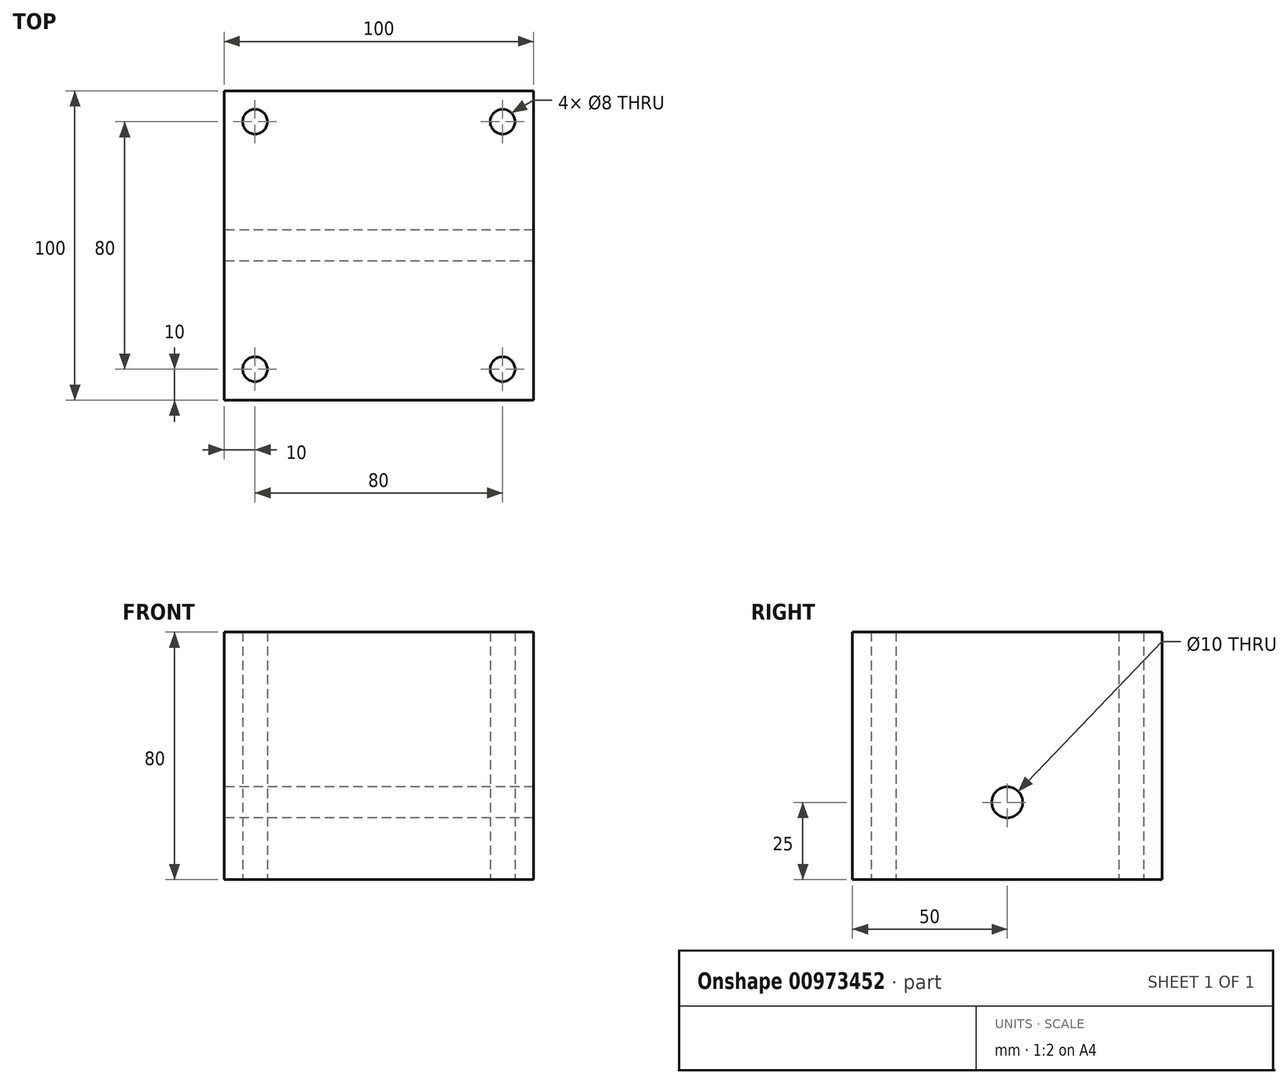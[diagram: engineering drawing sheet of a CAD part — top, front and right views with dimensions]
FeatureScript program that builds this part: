
annotation { "Feature Type Name" : "Feature", "Feature Type Description" : "" }
export const myFeature = defineFeature(function(context is Context, id is Id, definition is map)
    precondition{}
    {
        {
            var Q0;
            Q0=qCreatedBy(makeId("Top.planeOp"),FACE);
            var sketch = newSketch(context, id + "F0", { "sketchPlane" : qUnion([Q0])});
            skLineSegment(sketch, "E0.bottom", {"start": v(-50, 50) * mm, "end": v(50, 50) * mm});
            skLineSegment(sketch, "E0.top", {"start": v(-50, -50) * mm, "end": v(50, -50) * mm});
            skLineSegment(sketch, "E0.left", {"start": v(-50, 50) * mm, "end": v(-50, -50) * mm});
            skLineSegment(sketch, "E0.right", {"start": v(50, 50) * mm, "end": v(50, -50) * mm});
            skPoint(sketch, "E0.middle", {"position": v(0, 0) * mm});
            skSolve(sketch);
        }
        {
            var Q0;
            Q0=makeQuery(id+"F0.imprint","IMPRINT",FACE,{"disambiguationData":[TD([[makeQuery(id+"F0.imprint","IMPRINT",EDGE,{"derivedFrom":sQuery(id+"F0.wireOp",EDGE,"E0.bottom")}),-1.0]])]});
            extrude(context, id + "F1", {"entities" : qUnion([Q0]), "depth" : 50 * mm, "offsetDistance" : 25 * mm});
        }
        {
            var Q0;
            Q0=makeQuery(id+"F1.opExtrude","CAP_FACE",FACE,{"disambiguationData":[OSD([sQuery(id+"F0.wireOp",EDGE,"E0.bottom"),sQuery(id+"F0.wireOp",EDGE,"E0.top"),sQuery(id+"F0.wireOp",EDGE,"E0.left"),sQuery(id+"F0.wireOp",EDGE,"E0.right")])],"isStart":false});
            var sketch = newSketch(context, id + "F2", { "sketchPlane" : qUnion([Q0])});
            skCircle(sketch, "E1", {"center": v(-40, 40) * mm, "radius": 4 * mm});
            skCircle(sketch, "E2", {"center": v(40, 40) * mm, "radius": 4 * mm});
            skCircle(sketch, "E3", {"center": v(-40, -40) * mm, "radius": 4 * mm});
            skCircle(sketch, "E4", {"center": v(40, -40) * mm, "radius": 4 * mm});
            skSolve(sketch);
        }
        {
            var Q0;
            Q0=makeQuery(id+"F2.imprint","IMPRINT",FACE,{"disambiguationData":[TD([[makeQuery(id+"F2.imprint","IMPRINT",EDGE,{"derivedFrom":sQuery(id+"F2.wireOp",EDGE,"E1")}),-1.0]])]});
            extrude(context, id + "F3", {"entities" : qUnion([Q0]), "operationType" : NewBodyOperationType.ADD, "depth" : 30 * mm, "offsetDistance" : 25 * mm});
        }
        {
            var Q0;
            Q0=makeQuery(id+"F3.boolean.opBoolean","SPLIT",FACE,{"disambiguationData":[TD([makeQuery(id+"F3.opExtrude","SWEPT_FACE",FACE,{"disambiguationData":[OSD([sQuery(id+"F2.wireOp",EDGE,"E1")])]})])],"derivedFrom":makeQuery(id+"F1.opExtrude","CAP_FACE",FACE,{"disambiguationData":[OSD([sQuery(id+"F0.wireOp",EDGE,"E0.bottom"),sQuery(id+"F0.wireOp",EDGE,"E0.top"),sQuery(id+"F0.wireOp",EDGE,"E0.left"),sQuery(id+"F0.wireOp",EDGE,"E0.right")])],"isStart":false})});
            var Q1;
            Q1=makeQuery(id+"F3.boolean.opBoolean","SPLIT",FACE,{"disambiguationData":[TD([makeQuery(id+"F3.opExtrude","SWEPT_FACE",FACE,{"disambiguationData":[OSD([sQuery(id+"F2.wireOp",EDGE,"E2")])]})])],"derivedFrom":makeQuery(id+"F1.opExtrude","CAP_FACE",FACE,{"disambiguationData":[OSD([sQuery(id+"F0.wireOp",EDGE,"E0.bottom"),sQuery(id+"F0.wireOp",EDGE,"E0.top"),sQuery(id+"F0.wireOp",EDGE,"E0.left"),sQuery(id+"F0.wireOp",EDGE,"E0.right")])],"isStart":false})});
            var Q2;
            Q2=makeQuery(id+"F3.boolean.opBoolean","SPLIT",FACE,{"disambiguationData":[TD([makeQuery(id+"F3.opExtrude","SWEPT_FACE",FACE,{"disambiguationData":[OSD([sQuery(id+"F2.wireOp",EDGE,"E4")])]})])],"derivedFrom":makeQuery(id+"F1.opExtrude","CAP_FACE",FACE,{"disambiguationData":[OSD([sQuery(id+"F0.wireOp",EDGE,"E0.bottom"),sQuery(id+"F0.wireOp",EDGE,"E0.top"),sQuery(id+"F0.wireOp",EDGE,"E0.left"),sQuery(id+"F0.wireOp",EDGE,"E0.right")])],"isStart":false})});
            var Q3;
            Q3=makeQuery(id+"F3.boolean.opBoolean","SPLIT",FACE,{"disambiguationData":[TD([makeQuery(id+"F3.opExtrude","SWEPT_FACE",FACE,{"disambiguationData":[OSD([sQuery(id+"F2.wireOp",EDGE,"E3")])]})])],"derivedFrom":makeQuery(id+"F1.opExtrude","CAP_FACE",FACE,{"disambiguationData":[OSD([sQuery(id+"F0.wireOp",EDGE,"E0.bottom"),sQuery(id+"F0.wireOp",EDGE,"E0.top"),sQuery(id+"F0.wireOp",EDGE,"E0.left"),sQuery(id+"F0.wireOp",EDGE,"E0.right")])],"isStart":false})});
            extrude(context, id + "F4", {"entities" : qUnion([Q0, Q1, Q2, Q3]), "operationType" : NewBodyOperationType.REMOVE, "endBound" : BoundingType.THROUGH_ALL, "oppositeDirection" : true, "depth" : 25 * mm, "offsetDistance" : 25 * mm});
        }
        {
            var Q0;
            {var subQ0=sQuery(id+"F0.wireOp",EDGE,"E0.left");Q0=makeQuery(id+"F3.boolean.opBoolean","MERGE",FACE,{"derivedFrom":[makeQuery(id+"F1.opExtrude","SWEPT_FACE",FACE,{"disambiguationData":[OSD([subQ0])]}),makeQuery(id+"F3.opExtrude","SWEPT_FACE",FACE,{"disambiguationData":[OSD([subQ0])]})]});}
            var sketch = newSketch(context, id + "F5", { "sketchPlane" : qUnion([Q0])});
            skCircle(sketch, "E5", {"center": v(0, 25) * mm, "radius": 5 * mm});
            skSolve(sketch);
        }
        {
            var Q0;
            Q0=makeQuery(id+"F5.imprint","IMPRINT",FACE,{"disambiguationData":[TD([[makeQuery(id+"F5.imprint","IMPRINT",EDGE,{"derivedFrom":sQuery(id+"F5.wireOp",EDGE,"E5")}),1.0]])]});
            extrude(context, id + "F6", {"entities" : qUnion([Q0]), "operationType" : NewBodyOperationType.REMOVE, "endBound" : BoundingType.THROUGH_ALL, "oppositeDirection" : true, "depth" : 25 * mm, "offsetDistance" : 25 * mm});
        }
    });
